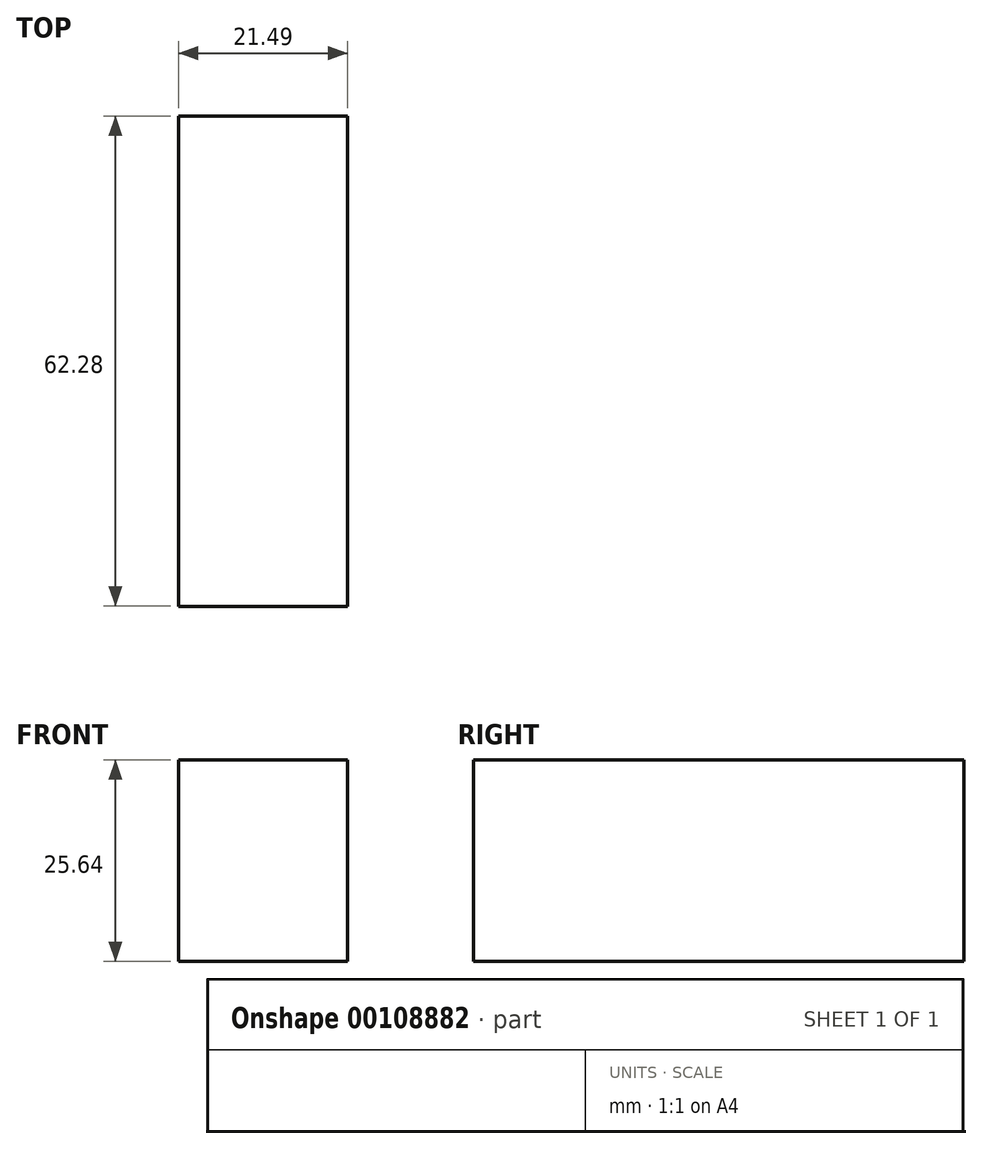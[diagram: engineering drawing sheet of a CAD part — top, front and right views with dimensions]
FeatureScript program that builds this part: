
annotation { "Feature Type Name" : "Feature", "Feature Type Description" : "" }
export const myFeature = defineFeature(function(context is Context, id is Id, definition is map)
    precondition{}
    {
        {
            var Q0;
            Q0=qCreatedBy(makeId("Front.planeOp"),FACE);
            var sketch = newSketch(context, id + "F0", { "sketchPlane" : qUnion([Q0])});
            skLineSegment(sketch, "E0.bottom", {"start": v(-66.35, 40.62) * mm, "end": v(-44.86, 40.62) * mm});
            skLineSegment(sketch, "E0.top", {"start": v(-66.35, 14.98) * mm, "end": v(-44.86, 14.98) * mm});
            skLineSegment(sketch, "E0.left", {"start": v(-66.35, 40.62) * mm, "end": v(-66.35, 14.98) * mm});
            skLineSegment(sketch, "E0.right", {"start": v(-44.86, 40.62) * mm, "end": v(-44.86, 14.98) * mm});
            skSolve(sketch);
        }
        {
            var Q0;
            Q0 = qSketchRegion(id + "F0", true);
            extrude(context, id + "F1", {"entities" : qUnion([Q0]), "depth" : 62.28 * mm});
        }
    });
